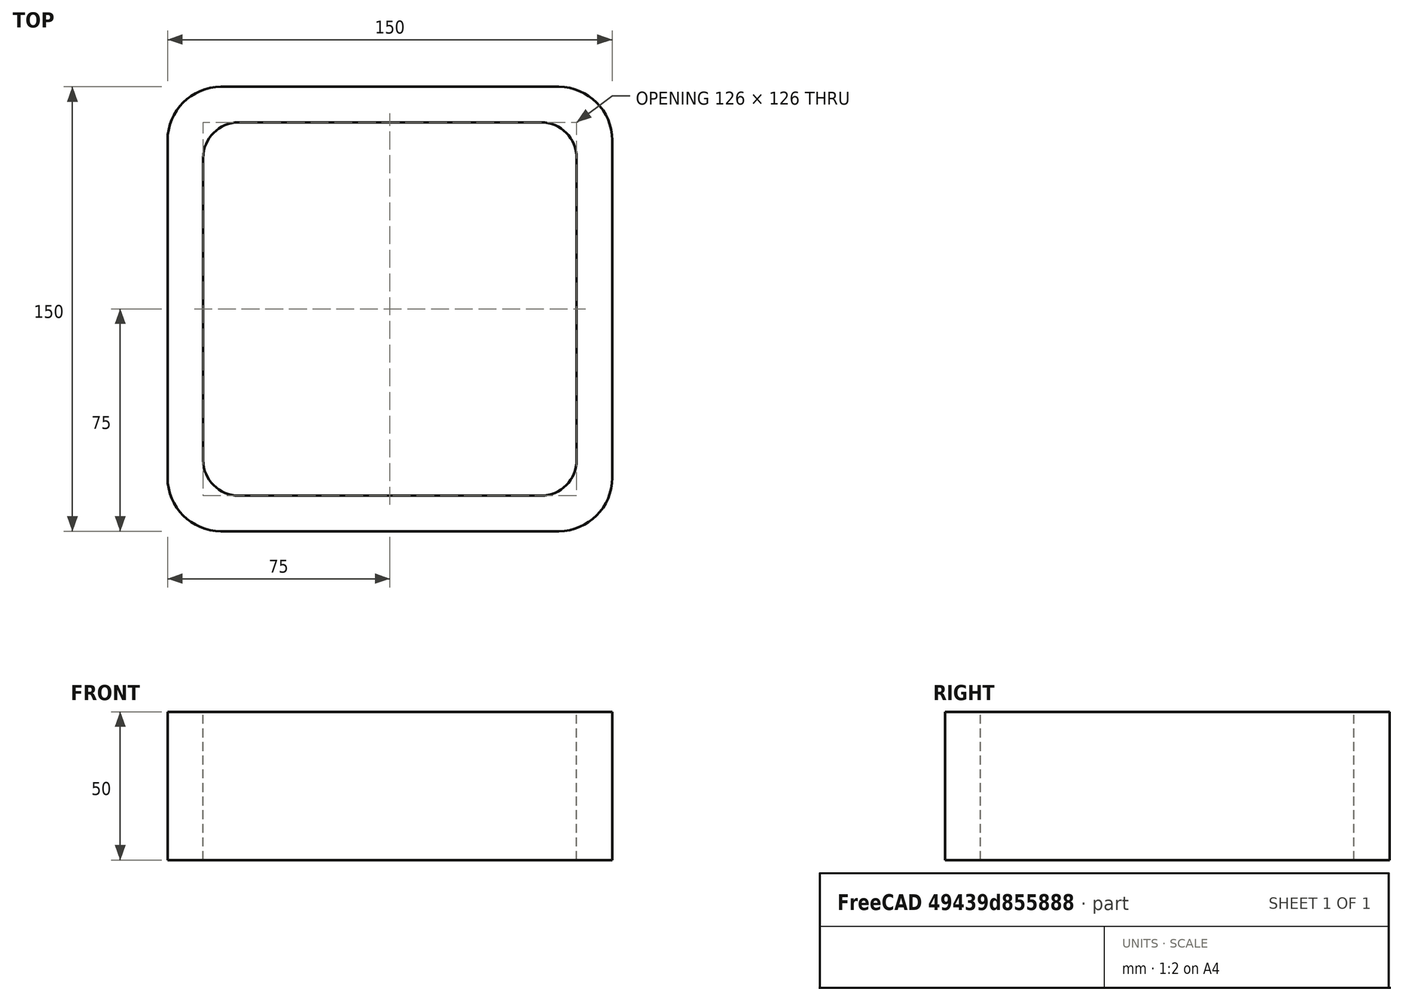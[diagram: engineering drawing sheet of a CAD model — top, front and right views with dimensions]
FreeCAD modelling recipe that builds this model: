
FCSTD DOCUMENT  (FreeCAD 0.15R4671 (Git))
Label: Square hollow section 150x150x12 EN10219 S235JRH
License: All rights reserved
LicenseURL: http://en.wikipedia.org/wiki/All_rights_reserved
objects: Sketcher::SketchObject×1, Part::Extrusion×1
note: 2 computed .brp shape members not serialized (recipe doc carries the construction recipe); baked Part::Feature solids carry a one-line shape summary decoded from their .brp

FEATURE [Sketcher::SketchObject] Sketch
  sketch-geometry (16):
    g0: LineSegment StartX=-51 StartY=63 StartZ=0 EndX=51 EndY=63 EndZ=0
    g1: LineSegment StartX=63 StartY=51 StartZ=0 EndX=63 EndY=-51 EndZ=0
    g2: LineSegment StartX=51 StartY=-63 StartZ=0 EndX=-51 EndY=-63 EndZ=0
    g3: LineSegment StartX=-63 StartY=-51 StartZ=0 EndX=-63 EndY=51 EndZ=0
    g4: LineSegment StartX=-57 StartY=75 StartZ=0 EndX=57 EndY=75 EndZ=0
    g5: LineSegment StartX=75 StartY=57 StartZ=0 EndX=75 EndY=-57 EndZ=0
    g6: LineSegment StartX=57 StartY=-75 StartZ=0 EndX=-57 EndY=-75 EndZ=0
    g7: LineSegment StartX=-75 StartY=-57 StartZ=0 EndX=-75 EndY=57 EndZ=0
    g8: ArcOfCircle CenterX=-51 CenterY=51 CenterZ=0 NormalX=0 NormalY=0 NormalZ=1 Radius=12 StartAngle=1.5708 EndAngle=3.14159
    g9: ArcOfCircle CenterX=51 CenterY=51 CenterZ=0 NormalX=0 NormalY=0 NormalZ=1 Radius=12 StartAngle=0 EndAngle=1.5708
    g10: ArcOfCircle CenterX=51 CenterY=-51 CenterZ=0 NormalX=0 NormalY=0 NormalZ=1 Radius=12 StartAngle=4.71239 EndAngle=6.28319
    g11: ArcOfCircle CenterX=-51 CenterY=-51 CenterZ=0 NormalX=0 NormalY=0 NormalZ=1 Radius=12 StartAngle=3.14159 EndAngle=4.71239
    g12: ArcOfCircle CenterX=57 CenterY=57 CenterZ=0 NormalX=0 NormalY=0 NormalZ=1 Radius=18 StartAngle=0 EndAngle=1.5708
    g13: ArcOfCircle CenterX=57 CenterY=-57 CenterZ=0 NormalX=0 NormalY=0 NormalZ=1 Radius=18 StartAngle=4.71239 EndAngle=6.28319
    g14: ArcOfCircle CenterX=-57 CenterY=-57 CenterZ=0 NormalX=0 NormalY=0 NormalZ=1 Radius=18 StartAngle=3.14159 EndAngle=4.71239
    g15: ArcOfCircle CenterX=-57 CenterY=57 CenterZ=0 NormalX=0 NormalY=0 NormalZ=1 Radius=18 StartAngle=1.5708 EndAngle=3.14159
  constraints (36):
    c: Horizontal(g2)
    c: Vertical(g3)
    c: Horizontal(g6)
    c: Vertical(g7)
    c: Tangent(g3,g8) = 1.5708
    c: Tangent(g0,g8) = 1.5708
    c: Tangent(g0,g9) = 1.5708
    c: Tangent(g1,g9) = 1.5708
    c: Tangent(g1,g10) = 1.5708
    c: Tangent(g2,g10) = 1.5708
    c: Tangent(g2,g11) = 1.5708
    c: Tangent(g3,g11) = 1.5708
    c: Tangent(g4,g12) = 1.5708
    c: Tangent(g5,g12) = 1.5708
    c: Tangent(g5,g13) = 1.5708
    c: Tangent(g6,g13) = 1.5708
    c: Tangent(g6,g14) = 1.5708
    c: Tangent(g7,g14) = 1.5708
    c: Tangent(g7,g15) = 1.5708
    c: Tangent(g4,g15) = 1.5708
    c: Equal(g9,g8)
    c: Equal(g9,g11)
    c: Equal(g9,g10)
    c: Equal(g12,g15)
    c: Equal(g12,g14)
    c: Equal(g12,g13)
    c: Symmetric(g4,g6,g-1)
    c: Symmetric(g7,g5,g-2)
    c: DistanceY(g4,g6) = -150
    c: DistanceX(g7,g5) = 150
    c: Symmetric(g3,g1,g-2)
    c: Symmetric(g0,g2,g-1)
    c: DistanceY(g0,g4) = 12
    c: DistanceX(g5,g1) = -12
    c: Radius(g9) = 12
    c: Radius(g12) = 18
FEATURE [Part::Extrusion] Extrude  label="Square hollow section 150x150x12 EN10219 S235JRH"
  Base = -> Sketch
  Dir = (0,0,50)
  Solid = true
